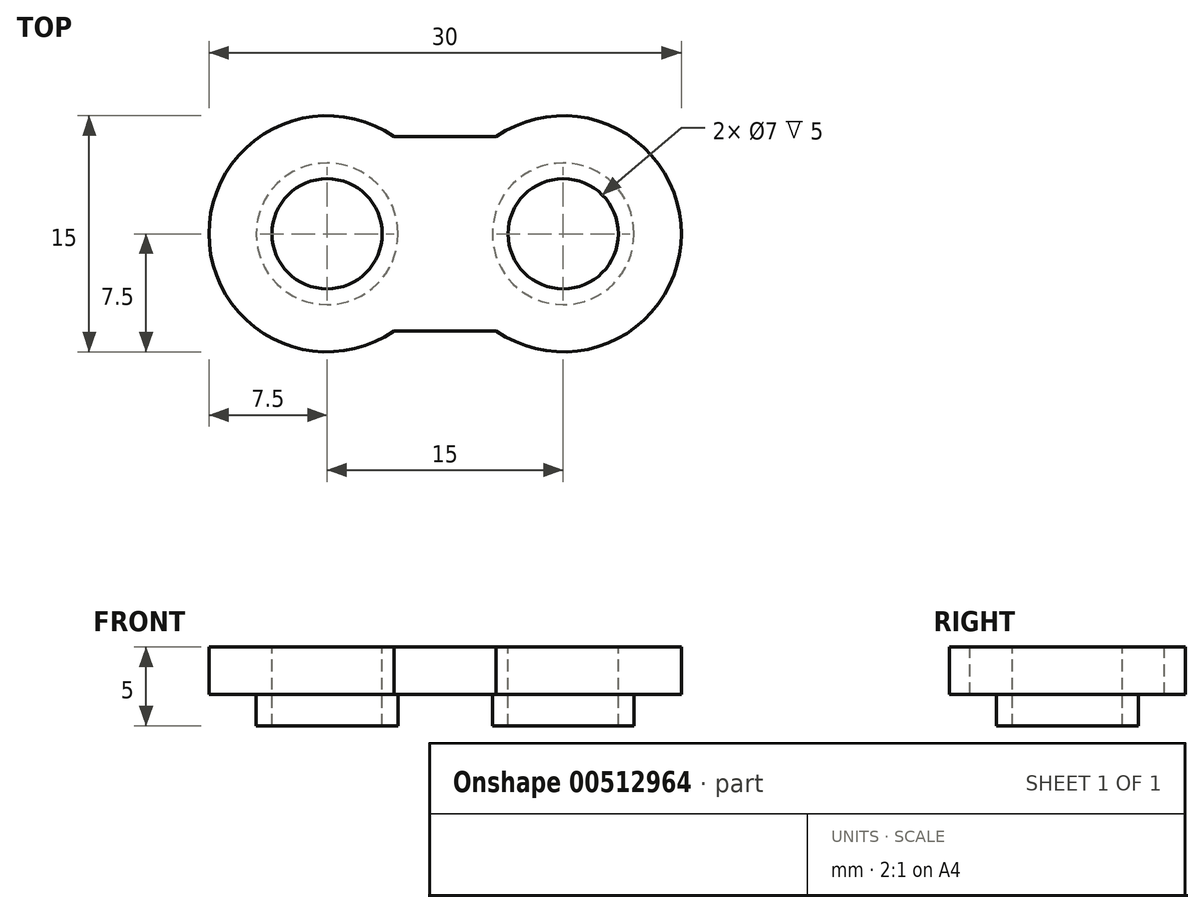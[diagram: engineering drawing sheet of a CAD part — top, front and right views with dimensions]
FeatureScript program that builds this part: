
annotation { "Feature Type Name" : "Feature", "Feature Type Description" : "" }
export const myFeature = defineFeature(function(context is Context, id is Id, definition is map)
    precondition{}
    {
        {
            var Q0;
            Q0=qCreatedBy(makeId("Top.planeOp"),FACE);
            var sketch = newSketch(context, id + "F0", { "sketchPlane" : qUnion([Q0])});
            skLineSegment(sketch, "E0.bottom", {"start": v(-3.24, 6.18) * mm, "end": v(3.24, 6.18) * mm});
            skLineSegment(sketch, "E0.top", {"start": v(-3.24, -6.18) * mm, "end": v(3.24, -6.18) * mm});
            skPoint(sketch, "E0.middle", {"position": v(0, 0) * mm});
            skCircle(sketch, "E1", {"center": v(-7.5, 0) * mm, "radius": 7.5 * mm});
            skCircle(sketch, "E2", {"center": v(7.5, 0) * mm, "radius": 7.5 * mm});
            skPoint(sketch, "E3.orphan", {"position": v(-7.25, 6.18) * mm});
            skPoint(sketch, "E4.orphan", {"position": v(-7.75, -6.18) * mm});
            skPoint(sketch, "E5.orphan", {"position": v(7.25, -6.18) * mm});
            skPoint(sketch, "E6.orphan", {"position": v(7.75, 6.18) * mm});
            skCircle(sketch, "E7", {"center": v(-7.5, 0) * mm, "radius": 4.5 * mm});
            skCircle(sketch, "E8", {"center": v(7.5, 0) * mm, "radius": 4.5 * mm});
            skCircle(sketch, "E9", {"center": v(-7.5, 0) * mm, "radius": 3.5 * mm});
            skCircle(sketch, "E10", {"center": v(7.5, 0) * mm, "radius": 3.5 * mm});
            skSolve(sketch);
        }
        {
            var Q0;
            Q0=makeQuery(id+"F0.imprint","IMPRINT",FACE,{"disambiguationData":[TD([[makeQuery(id+"F0.imprint","IMPRINT",EDGE,{"derivedFrom":sQuery(id+"F0.wireOp",EDGE,"E7")}),-1.0]])]});
            var Q1;
            Q1=makeQuery(id+"F0.imprint","IMPRINT",FACE,{"disambiguationData":[TD([[makeQuery(id+"F0.imprint","IMPRINT",EDGE,{"derivedFrom":sQuery(id+"F0.wireOp",EDGE,"E8")}),-1.0]])]});
            var Q2;
            {var subQ0=sQuery(id+"F0.wireOp",EDGE,"E0.bottom");Q2=makeQuery(id+"F0.imprint","IMPRINT",FACE,{"disambiguationData":[TD([[makeQuery(id+"F0.imprint","IMPRINT",EDGE,{"derivedFrom":subQ0}),-1.0]])]});}
            var Q3;
            {var subQ0=sQuery(id+"F0.wireOp",EDGE,"E0.top");Q3=makeQuery(id+"F0.imprint","IMPRINT",FACE,{"disambiguationData":[TD([[makeQuery(id+"F0.imprint","IMPRINT",EDGE,{"derivedFrom":subQ0}),1.0]])]});}
            extrude(context, id + "F1", {"entities" : qUnion([Q0, Q1, Q2, Q3]), "oppositeDirection" : true, "depth" : 3 * mm, "offsetDistance" : 25 * mm});
        }
        {
            var Q0;
            Q0=makeQuery(id+"F0.imprint","IMPRINT",FACE,{"disambiguationData":[TD([[makeQuery(id+"F0.imprint","IMPRINT",EDGE,{"derivedFrom":sQuery(id+"F0.wireOp",EDGE,"E8")}),1.0]])]});
            var Q1;
            Q1=makeQuery(id+"F0.imprint","IMPRINT",FACE,{"disambiguationData":[TD([[makeQuery(id+"F0.imprint","IMPRINT",EDGE,{"derivedFrom":sQuery(id+"F0.wireOp",EDGE,"E7")}),1.0]])]});
            extrude(context, id + "F2", {"entities" : qUnion([Q0, Q1]), "operationType" : NewBodyOperationType.ADD, "oppositeDirection" : true, "depth" : 5 * mm, "offsetDistance" : 25 * mm});
        }
    });
